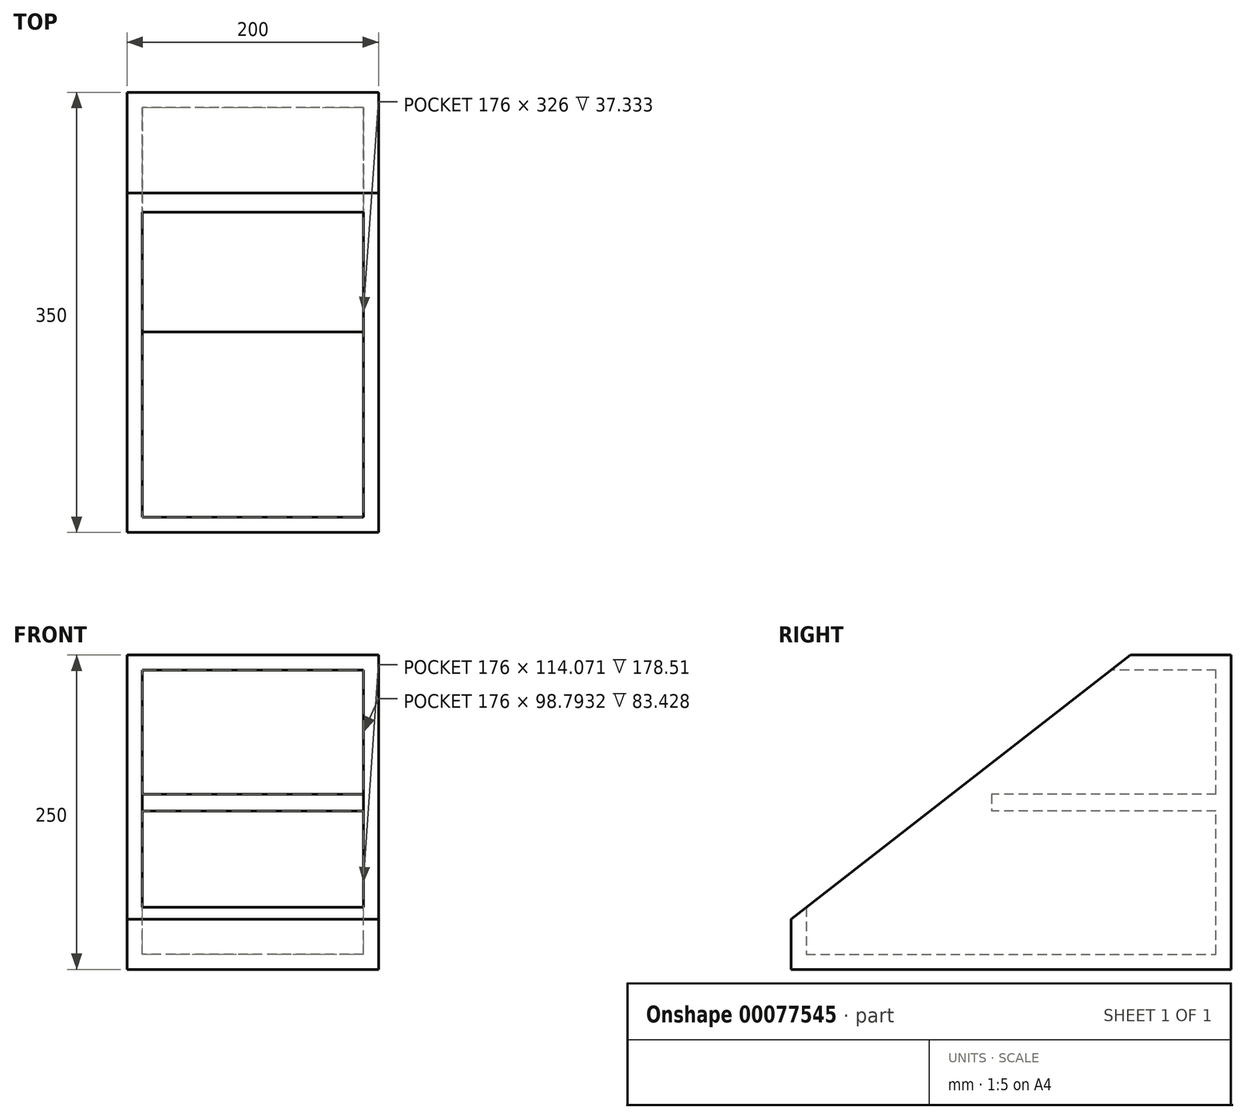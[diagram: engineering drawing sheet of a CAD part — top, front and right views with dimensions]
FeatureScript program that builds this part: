
annotation { "Feature Type Name" : "Feature", "Feature Type Description" : "" }
export const myFeature = defineFeature(function(context is Context, id is Id, definition is map)
    precondition{}
    {
        {
            var Q0;
            Q0=qCreatedBy(makeId("Right.planeOp"),FACE);
            var sketch = newSketch(context, id + "F0", { "sketchPlane" : qUnion([Q0])});
            skLineSegment(sketch, "E0", {"start": v(-193.73, -126.07) * mm, "end": v(156.27, -126.07) * mm});
            skLineSegment(sketch, "E1", {"start": v(156.27, -126.07) * mm, "end": v(156.27, 123.93) * mm});
            skLineSegment(sketch, "E2", {"start": v(156.27, 123.93) * mm, "end": v(76.27, 123.93) * mm});
            skLineSegment(sketch, "E3", {"start": v(76.27, 123.93) * mm, "end": v(-193.73, -86.07) * mm});
            skLineSegment(sketch, "E4", {"start": v(-193.73, -86.07) * mm, "end": v(-193.73, -126.07) * mm});
            skSolve(sketch);
        }
        {
            var Q0;
            Q0=makeQuery(id+"F0.imprint","IMPRINT",FACE,{"disambiguationData":[TD([[makeQuery(id+"F0.imprint","IMPRINT",EDGE,{"derivedFrom":sQuery(id+"F0.wireOp",EDGE,"E0")}),1.0]])]});
            extrude(context, id + "F1", {"entities" : qUnion([Q0]), "endBound" : BoundingType.SYMMETRIC, "depth" : 200 * mm});
        }
        {
            var Q0;
            Q0=makeQuery(id+"F1.opExtrude","SWEPT_FACE",FACE,{"disambiguationData":[OSD([sQuery(id+"F0.wireOp",EDGE,"E3")])]});
            shell(context, id + "F2", {"entities" : qUnion([Q0]), "thickness" : 12 * mm});
        }
        {
            var Q0;
            {var subQ0=sQuery(id+"F0.wireOp",EDGE,"E4");var subQ1=sQuery(id+"F0.wireOp",EDGE,"E3");var subQ2=sQuery(id+"F0.wireOp",EDGE,"E2");var subQ3=sQuery(id+"F0.wireOp",EDGE,"E1");var subQ4=sQuery(id+"F0.wireOp",EDGE,"E0");Q0=makeQuery(id+"F2.opShell","OFFSET_FACE",FACE,{"disambiguationData":[OSD([subQ4,subQ3,subQ2,subQ1,subQ0]),TDD([makeQuery(id+"F1.opExtrude","CAP_FACE",FACE,{"disambiguationData":[OSD([subQ4,subQ3,subQ2,subQ1,subQ0])],"isStart":true})])]});}
            cPlane(context, id + "F3", {"entities" : qUnion([Q0]), "cplaneType" : CPlaneType.OFFSET, "offset" : 150 * mm, "width" : 150 * mm, "height" : 150 * mm});
        }
        {
            var Q0;
            Q0=makeQuery(id+"F1.opExtrude","CAP_FACE",FACE,{"disambiguationData":[OSD([sQuery(id+"F0.wireOp",EDGE,"E0"),sQuery(id+"F0.wireOp",EDGE,"E1"),sQuery(id+"F0.wireOp",EDGE,"E2"),sQuery(id+"F0.wireOp",EDGE,"E3"),sQuery(id+"F0.wireOp",EDGE,"E4")])],"isStart":false});
            var sketch = newSketch(context, id + "F4", { "sketchPlane" : qUnion([Q0])});
            skLineSegment(sketch, "E5.bottom", {"start": v(153.45, 13.14) * mm, "end": v(-34.24, 13.14) * mm});
            skLineSegment(sketch, "E5.top", {"start": v(153.45, 0) * mm, "end": v(-34.24, 0) * mm});
            skLineSegment(sketch, "E5.left", {"start": v(153.45, 13.14) * mm, "end": v(153.45, 0) * mm});
            skLineSegment(sketch, "E5.right", {"start": v(-34.24, 13.14) * mm, "end": v(-34.24, 0) * mm});
            skSolve(sketch);
        }
        {
            var Q0;
            Q0 = qSketchRegion(id + "F4", true);
            var Q1;
            Q1=makeQuery(id+"F4.imprint","IMPRINT",FACE,{"disambiguationData":[TD([[makeQuery(id+"F4.imprint","IMPRINT",EDGE,{"derivedFrom":sQuery(id+"F4.wireOp",EDGE,"E5.bottom")}),1.0]])]});
            extrude(context, id + "F5", {"entities" : qUnion([Q0, Q1]), "operationType" : NewBodyOperationType.ADD, "oppositeDirection" : true, "depth" : 200 * mm});
        }
    });
